# Revit family: НЕВАТОМ_Регулятор расхода воздуха(РРВ), Версия 1
name_source: partatom
category: Арматура воздуховодов
revit_build: Autodesk Revit 2017 (Build: 20170118_1100(x64)
units: mm (PartAtom-declared; Revit-internal decimal feet)

## family parameters
Всегда вертикально = Нет
На основе рабочей плоскости = Нет
Общий = Нет
При загрузке вырезать с полостями = Нет
Размер круглого соединителя = Использовать диаметр
Тип детали = Вставляется

## types (11) — shared parameters
ADSK_Единица измерения = шт
ADSK_Завод-изготовитель = НЕВАТОМ
ADSK_Масса_Текст = кг
ADSK_Материал наименование = Оцинкованная сталь
ADSK_Наименование = Регулятор расхода воздуха(РРВ)
ADSK_Потеря давления воздуха = 0.0 Па
ADSK_Размер_Толщина = 56 мм
ADSK_Расход воздуха = 0.0 м³/ч
Nevatom_URL = https://t.me
k = 10 мм
t = 2 мм
Группа модели = Вентиляция
Материал = Сталь оцинкованная
С = 56 мм
с = 11 мм
с1 = 8 мм
zero-valued in all types: ADSK_Количество, ADSK_Масса

## per-type parameters (varying)
| type | A | ADSK_Марка | ADSK_Размер_Длина | ADSK_Размер_Ширина | B | шаг |
| РРВ 100х100 | 100 мм |  | 100 мм | 100 мм | 100 мм | 30 мм |
| РРВ 150х150 | 150 мм | РРВ 150х150 | 150 мм | 150 мм | 150 мм | 30 мм |
| РРВ 200х200 | 200 мм | РРВ 200х200 | 200 мм | 200 мм | 200 мм | 30 мм |
| РРВ 250х250 | 250 мм | РРВ 250х250 | 250 мм | 250 мм | 250 мм | 28 мм |
| РРВ 300х300 | 300 мм | РРВ 300х300 | 300 мм | 300 мм | 300 мм | 28 мм |
| РРВ 350х350 | 350 мм | РРВ 350х350 | 350 мм | 350 мм | 350 мм | 25 мм |
| РРВ 400х400 | 400 мм | РРВ 400х400 | 400 мм | 400 мм | 400 мм | 25 мм |
| РРВ 450х450 | 450 мм | РРВ 450х450 | 450 мм | 450 мм | 450 мм | 24 мм |
| РРВ 500х500 | 500 мм | РРВ 500х500 | 500 мм | 500 мм | 500 мм | 25 мм |
| РРВ 550х550 | 500 мм | РРВ 550х550 | 500 мм | 500 мм | 500 мм | 23 мм |
| РРВ 600х600 | 600 мм | РРВ 600х600 | 600 мм | 600 мм | 600 мм | 24 мм |
